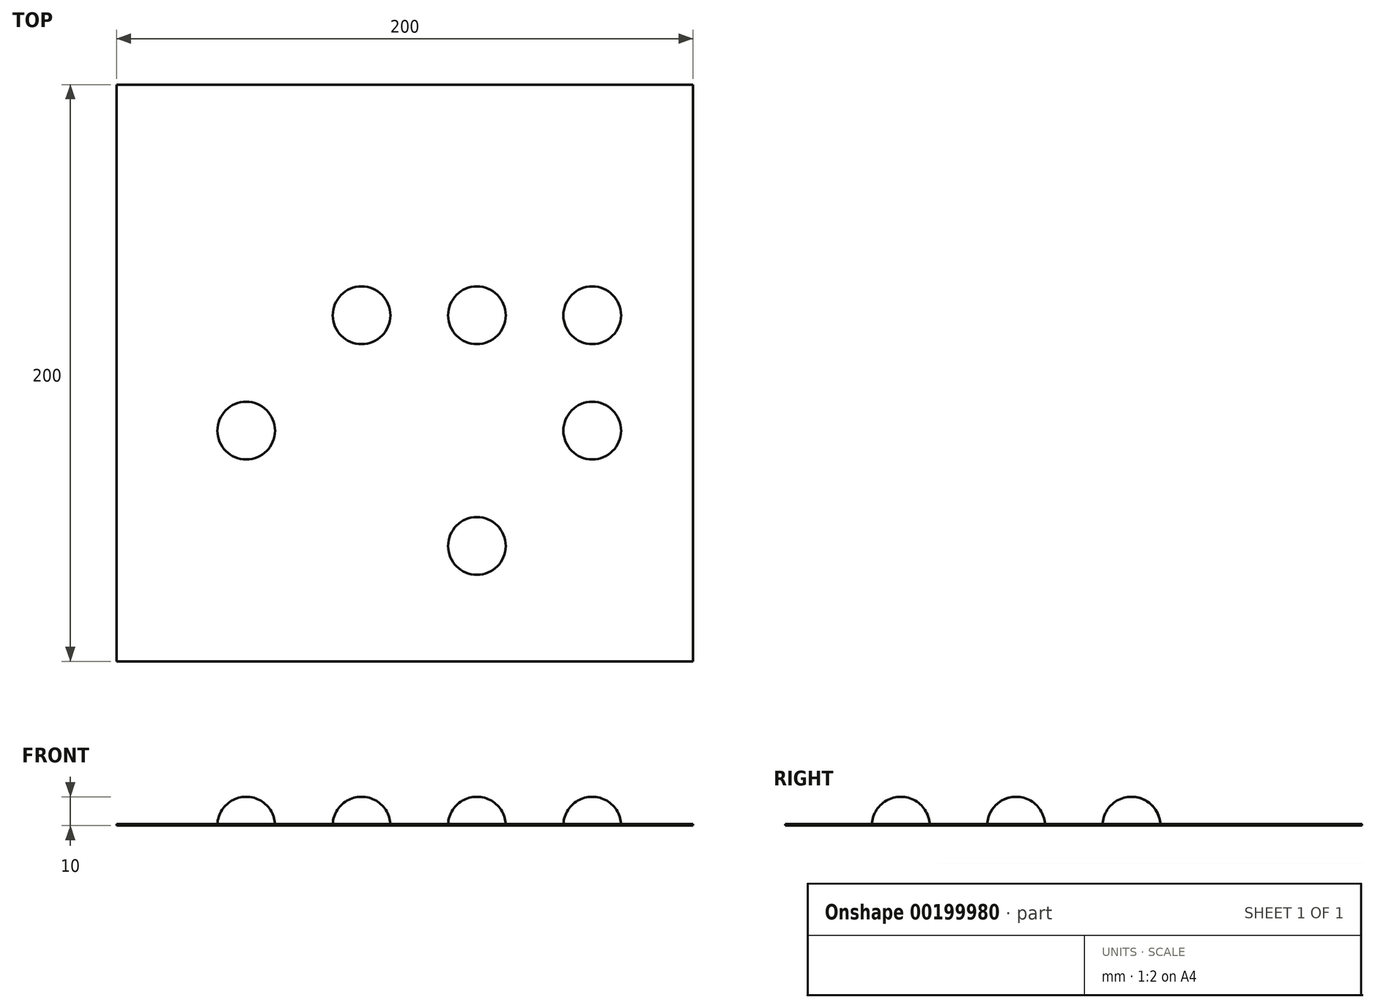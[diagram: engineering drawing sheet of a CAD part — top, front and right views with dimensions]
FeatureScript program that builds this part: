
annotation { "Feature Type Name" : "Feature", "Feature Type Description" : "" }
export const myFeature = defineFeature(function(context is Context, id is Id, definition is map)
    precondition{}
    {
        {
            var Q0;
            Q0=qCreatedBy(makeId("Top.planeOp"),FACE);
            var sketch = newSketch(context, id + "F0", { "sketchPlane" : qUnion([Q0])});
            skLineSegment(sketch, "E0.bottom", {"start": v(-100, 100) * mm, "end": v(100, 100) * mm});
            skLineSegment(sketch, "E0.top", {"start": v(-100, -100) * mm, "end": v(100, -100) * mm});
            skLineSegment(sketch, "E0.left", {"start": v(-100, 100) * mm, "end": v(-100, -100) * mm});
            skLineSegment(sketch, "E0.right", {"start": v(100, 100) * mm, "end": v(100, -100) * mm});
            skPoint(sketch, "E0.middle", {"position": v(0, 0) * mm});
            skSolve(sketch);
        }
        {
            var Q0;
            Q0=makeQuery(id+"F0.imprint","IMPRINT",FACE,{"disambiguationData":[TD([[makeQuery(id+"F0.imprint","IMPRINT",EDGE,{"derivedFrom":sQuery(id+"F0.wireOp",EDGE,"E0.bottom")}),-1.0]])]});
            var sketch = newSketch(context, id + "F1", { "sketchPlane" : qUnion([Q0])});
            skCircle(sketch, "E1.0.1.0", {"center": v(-55, -20) * mm, "radius": 10 * mm});
            skCircle(sketch, "E1.1.2.0", {"center": v(-15, 20) * mm, "radius": 10 * mm});
            skCircle(sketch, "E1.2.0.0", {"center": v(25, -60) * mm, "radius": 10 * mm});
            skCircle(sketch, "E1.2.2.0", {"center": v(25, 20) * mm, "radius": 10 * mm});
            skCircle(sketch, "E1.3.1.0", {"center": v(65, -20) * mm, "radius": 10 * mm});
            skCircle(sketch, "E1.3.2.0", {"center": v(65, 20) * mm, "radius": 10 * mm});
            skLineSegment(sketch, "E1.direction1", {"start": v(-55, -60) * mm, "end": v(-15, -60) * mm, "construction": true});
            skLineSegment(sketch, "E1.direction2", {"start": v(-55, -60) * mm, "end": v(-55, -20) * mm, "construction": true});
            skSolve(sketch);
        }
        {
            var Q0;
            Q0 = qSketchRegion(id + "F0", true);
            extrude(context, id + "F2", {"entities" : qUnion([Q0]), "depth" : 0.5 * mm});
        }
        {
            var Q0;
            Q0 = qSketchRegion(id + "F1", true);
            extrude(context, id + "F3", {"entities" : qUnion([Q0]), "operationType" : NewBodyOperationType.ADD, "depth" : 10 * mm});
        }
        {
            var Q0;
            Q0=makeQuery(id+"F3.opExtrude","CAP_EDGE",EDGE,{"disambiguationData":[OSD([sQuery(id+"F1.wireOp",EDGE,"E1.0.1.0")])],"isStart":false});
            var Q1;
            Q1=makeQuery(id+"F3.opExtrude","CAP_EDGE",EDGE,{"disambiguationData":[OSD([sQuery(id+"F1.wireOp",EDGE,"E1.1.2.0")])],"isStart":false});
            var Q2;
            Q2=makeQuery(id+"F3.opExtrude","CAP_EDGE",EDGE,{"disambiguationData":[OSD([sQuery(id+"F1.wireOp",EDGE,"E1.2.2.0")])],"isStart":false});
            var Q3;
            Q3=makeQuery(id+"F3.opExtrude","CAP_EDGE",EDGE,{"disambiguationData":[OSD([sQuery(id+"F1.wireOp",EDGE,"E1.3.2.0")])],"isStart":false});
            var Q4;
            Q4=makeQuery(id+"F3.opExtrude","CAP_EDGE",EDGE,{"disambiguationData":[OSD([sQuery(id+"F1.wireOp",EDGE,"E1.3.1.0")])],"isStart":false});
            var Q5;
            Q5=makeQuery(id+"F3.opExtrude","CAP_EDGE",EDGE,{"disambiguationData":[OSD([sQuery(id+"F1.wireOp",EDGE,"E1.2.0.0")])],"isStart":false});
            fillet(context, id + "F4", {"entities" : qUnion([Q0, Q1, Q2, Q3, Q4, Q5]), "radius" : 10 * mm, "tangentPropagation" : true, "allowEdgeOverflow" : false});
        }
    });
